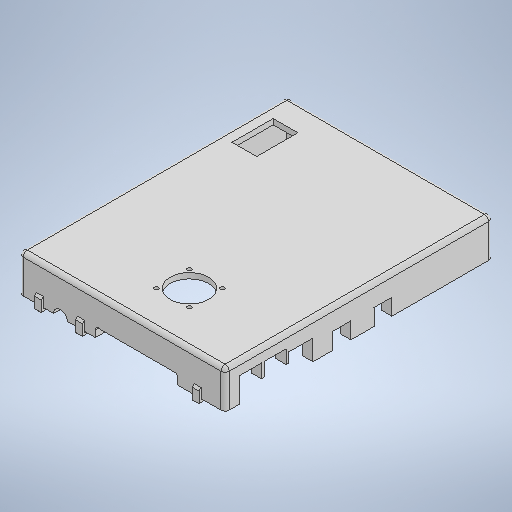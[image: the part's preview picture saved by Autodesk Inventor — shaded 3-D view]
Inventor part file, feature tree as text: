
AUTODESK INVENTOR PART (.ipt)
format: ipt  version: 2025.2 (Build 292293000, 293)  size: 688,640 bytes
history: native  units: mm
features: extrude x27, sketch x10, plane x5, fillet x4, shell x1, pattern_linear x1
ambient origin geometry x8: Origin, YZ Plane, XZ Plane, XY Plane, X Axis, Y Axis, Z Axis, Center Point
bodies: Solid1 (feature_tree)
feature tree (48):
  extrude  "Extrusion1"  Depth=7.5mm
  shell  "Shell1"  Thickness=135.0mm
  sketch  "Sketch2"  dims[d10=3.0mm d12=21.0mm]
  extrude  "Board Ports"  Depth=21.0mm
  extrude  "Extrusion9"  Depth=101.0mm
  fillet  "Fillet4"  Radius=13.0mm
  extrude  "Extrusion10"  Depth=180.0mm
  extrude  "Extrusion11"  Depth=87.0mm
  extrude  "Extrusion12"  Depth=3.0mm
  fillet  "Fillet1"  Radius=19.0mm
  plane  "Work Plane6"
  plane  "Work Plane7"
  plane  "Work Plane8"
  plane  "Work Plane9"
  sketch  "Sketch3"  dims[d16=70.5mm d18=101.0mm d19=13.0mm]
  extrude  "Extrusion3"  Depth=37.0mm
  extrude  "Extrusion25"  Depth=1.2mm
  extrude  "Extrusion8"  Depth=1.0mm
  extrude  "Extrusion26"  Depth=5.0mm TaperAngle=0.0deg
  extrude  "Extrusion5"  Depth=5.0mm TaperAngle=0.0deg
  extrude  "Extrusion27"  Depth=5.0mm TaperAngle=0.0deg
  extrude  "Extrusion6"  Depth=5.0mm TaperAngle=0.0deg
  extrude  "Extrusion28"  Depth=5.0mm TaperAngle=0.0deg
  extrude  "Extrusion7"  Depth=7.0mm TaperAngle=0.0deg
  extrude  "Extrusion29"  Depth=8.0mm TaperAngle=0.0deg
  extrude  "DC opening"  Depth=15.0mm TaperAngle=0.0deg
  plane  "Work Plane10"
  extrude  "Extrusion14"  Depth=12.0mm TaperAngle=0.0deg
  sketch  "Sketch9"  dims[d30=56.5mm d35=1.2mm]
  extrude  "DC Motor JST-PH slot"  [1 undecoded]
  extrude  "JST-PH slot reinforce"  [1 undecoded]
  extrude  "Material reduction"  [1 undecoded]
  pattern_linear  "Rectangular Pattern1"  Spacing1=-135.0mm  [1 undecoded]
  fillet  "Fillet2"  Radius=30.0mm
  fillet  "Fillet3"  [1 undecoded]
  sketch  "Sketch7"  dims[d24=18.0mm d25=0.0mm d26=3.0mm d27=19.0mm]
  extrude  "Motor driver heat sink hole"  Depth=10.0mm
  extrude  "Fan recess face"  Depth=27.0mm
  extrude  "Fan mounting holes"  Depth=10.5mm
  extrude  "Fan opening"  Depth=14.0mm
  extrude  "Extrusion17"  Depth=13.0mm
  extrude  "Extra cable slot"  Depth=6.0mm
  sketch  "Sketch1"  dims[d0=20.0mm d1=0.0mm d2=7.5mm d9=135.0mm]
  sketch  "Sketch4"  dims[d20=13.64mm d21=180.0mm]
  sketch  "Sketch5"  dims[d22=27.0mm d23=87.0mm]
  sketch  "Sketch8"  dims[d28=37.0mm d29=39.0mm]
  sketch  "Sketch10"  dims[d36=2.5mm d37=1.0mm]
  sketch  "Sketch11"  dims[d38=45.0deg d39=5.0mm d40=0.0mm d43=5.0mm d44=0.0mm d45=5.0mm d46=0.0mm d47=5.0mm d48=0.0mm d50=5.0mm d51=0.0mm d52=7.0mm d53=0.0mm d54=8.0mm d55=0.0mm d56=15.0mm d57=0.0mm d58=12.0mm d59=0.0mm d60=-20.0mm d61=-105.0mm d62=-130.0mm d63=-135.0mm d64=30.0mm d65=0.0mm d66=0.0mm d67=10.0mm d68=27.0mm d69=10.5mm d70=14.0mm d71=13.0mm d72=6.0mm d73=30.0mm d74=3.0mm d75=0.0mm d81=1.0mm d82=1.0mm d83=12.0mm d84=42.0mm d85=2.0mm d86=20.0mm d87=20.0mm d88=0.0mm d89=3.5mm d90=0.0mm d91=30.5mm d92=30.5mm d93=3.0mm d95=24.0mm d96=24.0mm d97=2.0mm d98=0.0mm d99=0.0mm d100=0.0mm d101=28.0mm d102=10.0mm d103=0.0mm d104=13.2mm d105=14.1mm d107=6.2mm d108=18.0mm d109=5.0mm d110=1.7mm d111=0.0mm d112=0.0mm d113=0.0mm d114=40.0mm d116=16.0mm d117=115.0mm d118=50.0mm d119=5.0mm d120=15.0mm d121=45.0deg d122=8.0mm d123=1.7mm d124=0.0mm d125=10.0mm d126=0.0mm d127=2.0mm d128=45.0deg d129=1.5mm d130=0.8mm d131=4.0mm d132=0.0mm d133=8.0mm d134=4.0mm d135=0.0mm d136=4.0mm d137=0.0mm d138=4.0mm d139=0.0mm d140=4.0mm d141=0.0mm]
note: 5 required parameter values undecoded (feature->parameter linkage not recoverable at this tier; creation-order binding heuristic only, values carry confidence <= 0.55)
